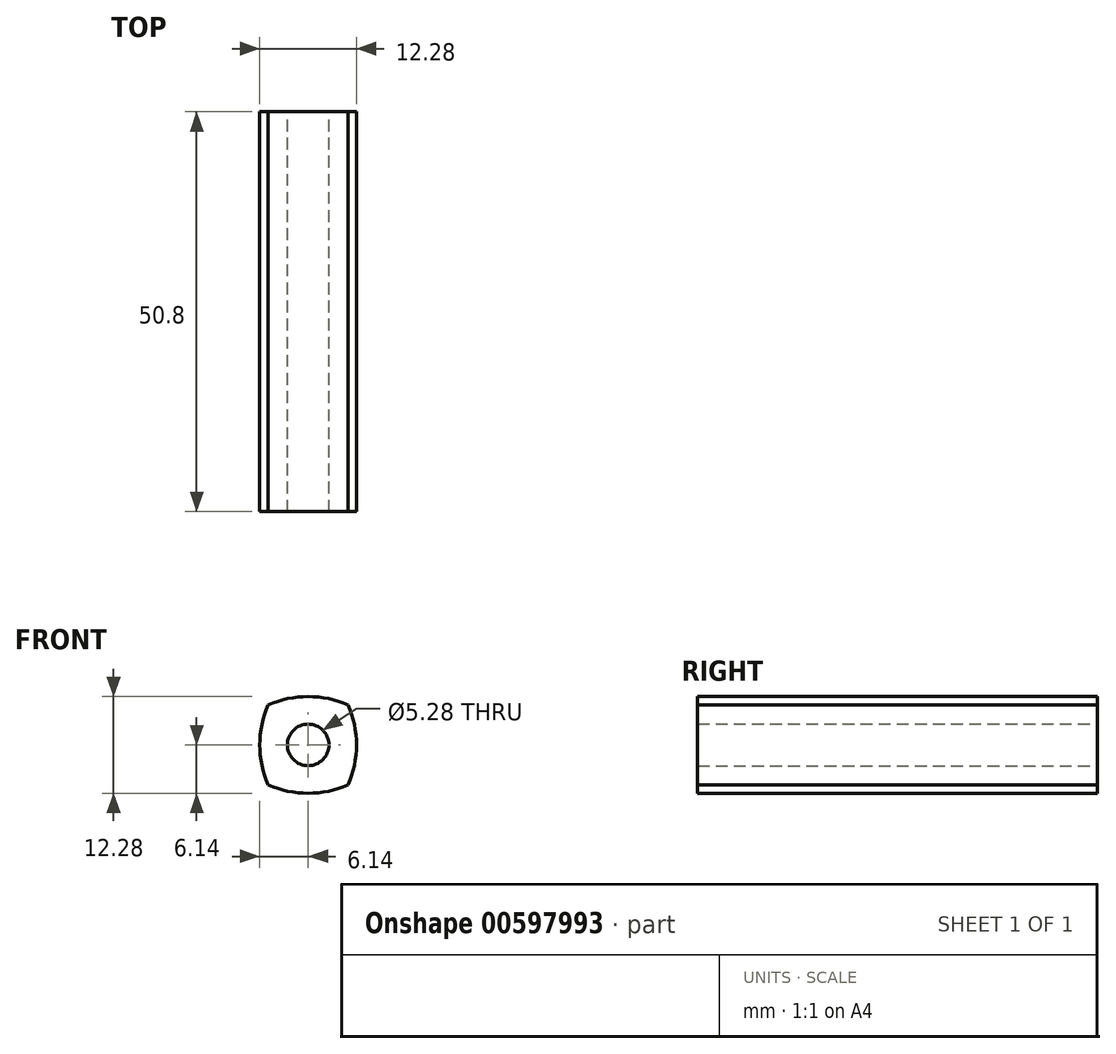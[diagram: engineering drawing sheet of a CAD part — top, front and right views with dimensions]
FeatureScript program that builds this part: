
annotation { "Feature Type Name" : "Feature", "Feature Type Description" : "" }
export const myFeature = defineFeature(function(context is Context, id is Id, definition is map)
    precondition{}
    {
        {
            var Q0;
            Q0=qCreatedBy(makeId("Front.planeOp"),FACE);
            var sketch = newSketch(context, id + "F0", { "sketchPlane" : qUnion([Q0])});
            skLineSegment(sketch, "E0.bottom", {"start": v(-5.08, 5.08) * mm, "end": v(5.08, 5.08) * mm});
            skLineSegment(sketch, "E0.top", {"start": v(-5.08, -5.08) * mm, "end": v(5.08, -5.08) * mm});
            skLineSegment(sketch, "E0.left", {"start": v(-5.08, 5.08) * mm, "end": v(-5.08, -5.08) * mm});
            skLineSegment(sketch, "E0.right", {"start": v(5.08, 5.08) * mm, "end": v(5.08, -5.08) * mm});
            skPoint(sketch, "E0.middle", {"position": v(0, 0) * mm});
            skCircle(sketch, "E1", {"center": v(0, 0) * mm, "radius": 2.64 * mm});
            skArc(sketch, "E2", {"start": v(-5.08, 5.08) * mm, "mid": v(-6.14, 0) * mm, "end": v(-5.08, -5.08) * mm});
            skArc(sketch, "E3", {"start": v(5.08, -5.08) * mm, "mid": v(6.14, 0) * mm, "end": v(5.08, 5.08) * mm});
            skArc(sketch, "E4", {"start": v(5.08, 5.08) * mm, "mid": v(0, 6.14) * mm, "end": v(-5.08, 5.08) * mm});
            skArc(sketch, "E5", {"start": v(-5.08, -5.08) * mm, "mid": v(0, -6.14) * mm, "end": v(5.08, -5.08) * mm});
            skSolve(sketch);
        }
        {
            var Q0;
            Q0=qSketchRegion(id+"F0",true);
            extrude(context, id + "F1", {"entities" : qUnion([Q0]), "depth" : 50.8 * mm, "offsetDistance" : 25.4 * mm});
        }
    });
